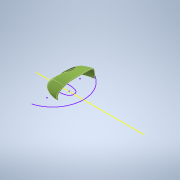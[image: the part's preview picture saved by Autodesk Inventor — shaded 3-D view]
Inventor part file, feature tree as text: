
AUTODESK INVENTOR PART (.ipt)
format: ipt  version: 2021 (Build 250183000, 183)  size: 3,075,072 bytes
history: native  units: mm
features: other x21, split x7, surface_op x7, sketch x6, extrude x2, plane x1, shell x1
ambient origin geometry x8: Origin, YZ Plane, XZ Plane, XY Plane, X Axis, Y Axis, Z Axis, Center Point
bodies: Solid2 (feature_tree), Solid3 (feature_tree), Solid4 (feature_tree), Solid5 (feature_tree), Solid6 (feature_tree)
feature tree (45):
  other  "CrossSection1"
  other  "Curvature1"
  sketch  "Sketch1"  dims[d1=120.0mm d5=60.0mm d6=7.0mm]
  sketch  "Sketch2"  dims[d9=120.0mm d13=42.0mm]
  other  "Form2"
  extrude  "Extrusion5"  Depth=60.0mm
  sketch  "Sketch9"  dims[d25=0.5mm d26=2.0mm d27=0.0mm d28=20.0mm]
  sketch  "3D Sketch1"
  split  "Split1"
  split  "Split2"
  plane  "Work Plane1"
  split  "Split3"
  other  "Ruled Surface1"
  surface_op  "Extend1"
  other  "Ruled Surface6"
  surface_op  "Extend2"
  other  "Ruled Surface7"
  surface_op  "Extend3"
  surface_op  "Stitch Surface1"
  other  "Ruled Surface8"
  surface_op  "Extend4"
  surface_op  "Stitch Surface2"
  split  "Split4"
  shell  "Shell1"  Thickness=7.0mm
  split  "Split5"
  surface_op  "Extend5"
  split  "Split6"
  split  "Split7"
  other  "Image1"
  other  "Image2"
  sketch  "Sketch8"  dims[d14=60.0mm]
  other  "Project to Surface1"
  other  "Srf1"
  other  "Srf2"
  other  "Srf7"
  other  "Srf8"
  other  "Srf9"
  other  "Srf10"
  other  "Srf11"
  other  "Srf12"
  sketch  "Sketch10"  dims[d41=1.0mm d44=48.0mm d45=0.0mm d46=8.0mm d47=3.0mm d48=3.0mm d49=10.0mm d50=0.0mm d51=3.0mm d62=10.0mm d63=0.0mm d64=3.0mm d65=10.0mm d66=0.0mm d67=3.0mm d68=10.0mm d69=0.0mm d70=3.0mm d71=1.3mm d72=1.3mm d73=1.3mm d74=4.0mm d75=1.0mm d76=100.0mm d77=0.0mm d30=0.5mm d31=0.872665mm d32=0.5mm d33=0.872665mm d34=0.872665mm d42=0.5mm d43=0.872665mm]
  other  "Srf13"
  other  "OffsetSrf1"
  other  "OffsetSrf2"
  extrude  "ExtrusionSrf1"  Depth=42.0mm
